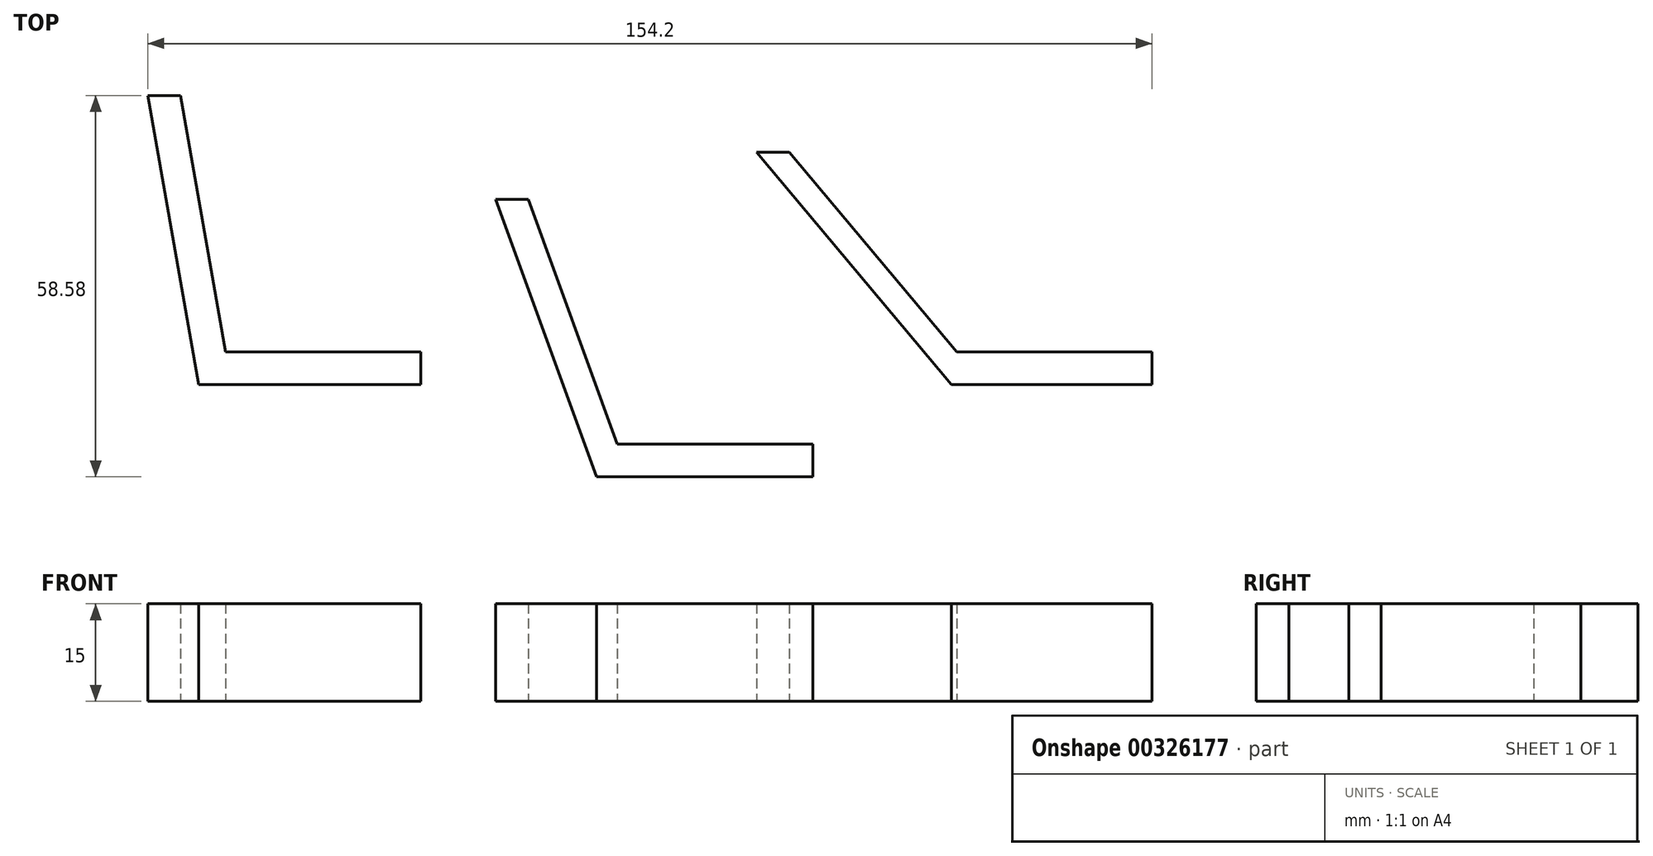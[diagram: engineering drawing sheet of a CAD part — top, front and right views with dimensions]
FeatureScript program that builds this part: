
annotation { "Feature Type Name" : "Feature", "Feature Type Description" : "" }
export const myFeature = defineFeature(function(context is Context, id is Id, definition is map)
    precondition{}
    {
        {
            var Q0;
            Q0=qCreatedBy(makeId("Top.planeOp"),FACE);
            var sketch = newSketch(context, id + "F0", { "sketchPlane" : qUnion([Q0])});
            skLineSegment(sketch, "E0", {"start": v(-65.1, 44.4) * mm, "end": v(-57.27, 0) * mm});
            skLineSegment(sketch, "E1", {"start": v(-57.27, 0) * mm, "end": v(-23.15, 0) * mm});
            skLineSegment(sketch, "E2", {"start": v(-23.15, 0) * mm, "end": v(-23.15, 5) * mm});
            skLineSegment(sketch, "E3", {"start": v(-23.15, 5) * mm, "end": v(-53.15, 5) * mm});
            skLineSegment(sketch, "E4", {"start": v(-53.15, 5) * mm, "end": v(-60.1, 44.4) * mm});
            skLineSegment(sketch, "E5", {"start": v(-60.1, 44.4) * mm, "end": v(-65.1, 44.4) * mm});
            skLineSegment(sketch, "E6", {"start": v(-11.68, 28.4) * mm, "end": v(3.82, -14.19) * mm});
            skLineSegment(sketch, "E7", {"start": v(3.82, -14.19) * mm, "end": v(37, -14.19) * mm});
            skLineSegment(sketch, "E8", {"start": v(37, -14.19) * mm, "end": v(37, -9.19) * mm});
            skLineSegment(sketch, "E9", {"start": v(37, -9.19) * mm, "end": v(7, -9.19) * mm});
            skLineSegment(sketch, "E10", {"start": v(7, -9.19) * mm, "end": v(-6.68, 28.4) * mm});
            skLineSegment(sketch, "E11", {"start": v(-6.68, 28.4) * mm, "end": v(-11.68, 28.4) * mm});
            skLineSegment(sketch, "E12", {"start": v(28.39, 35.64) * mm, "end": v(58.3, 0) * mm});
            skLineSegment(sketch, "E13", {"start": v(58.3, 0) * mm, "end": v(89.1, 0) * mm});
            skLineSegment(sketch, "E14", {"start": v(89.1, 0) * mm, "end": v(89.1, 5) * mm});
            skLineSegment(sketch, "E15", {"start": v(89.1, 5) * mm, "end": v(59.1, 5) * mm});
            skLineSegment(sketch, "E16", {"start": v(59.1, 5) * mm, "end": v(33.39, 35.64) * mm});
            skLineSegment(sketch, "E17", {"start": v(33.39, 35.64) * mm, "end": v(28.39, 35.64) * mm});
            skSolve(sketch);
        }
        {
            var Q0;
            Q0=makeQuery(id+"F0.imprint","IMPRINT",FACE,{"disambiguationData":[TD([[makeQuery(id+"F0.imprint","IMPRINT",EDGE,{"derivedFrom":sQuery(id+"F0.wireOp",EDGE,"E0")}),1.0]])]});
            var Q1;
            Q1=makeQuery(id+"F0.imprint","IMPRINT",FACE,{"disambiguationData":[TD([[makeQuery(id+"F0.imprint","IMPRINT",EDGE,{"derivedFrom":sQuery(id+"F0.wireOp",EDGE,"E6")}),1.0]])]});
            var Q2;
            Q2=makeQuery(id+"F0.imprint","IMPRINT",FACE,{"disambiguationData":[TD([[makeQuery(id+"F0.imprint","IMPRINT",EDGE,{"derivedFrom":sQuery(id+"F0.wireOp",EDGE,"E12")}),1.0]])]});
            extrude(context, id + "F1", {"entities" : qUnion([Q0, Q1, Q2]), "depth" : 15 * mm});
        }
    });
